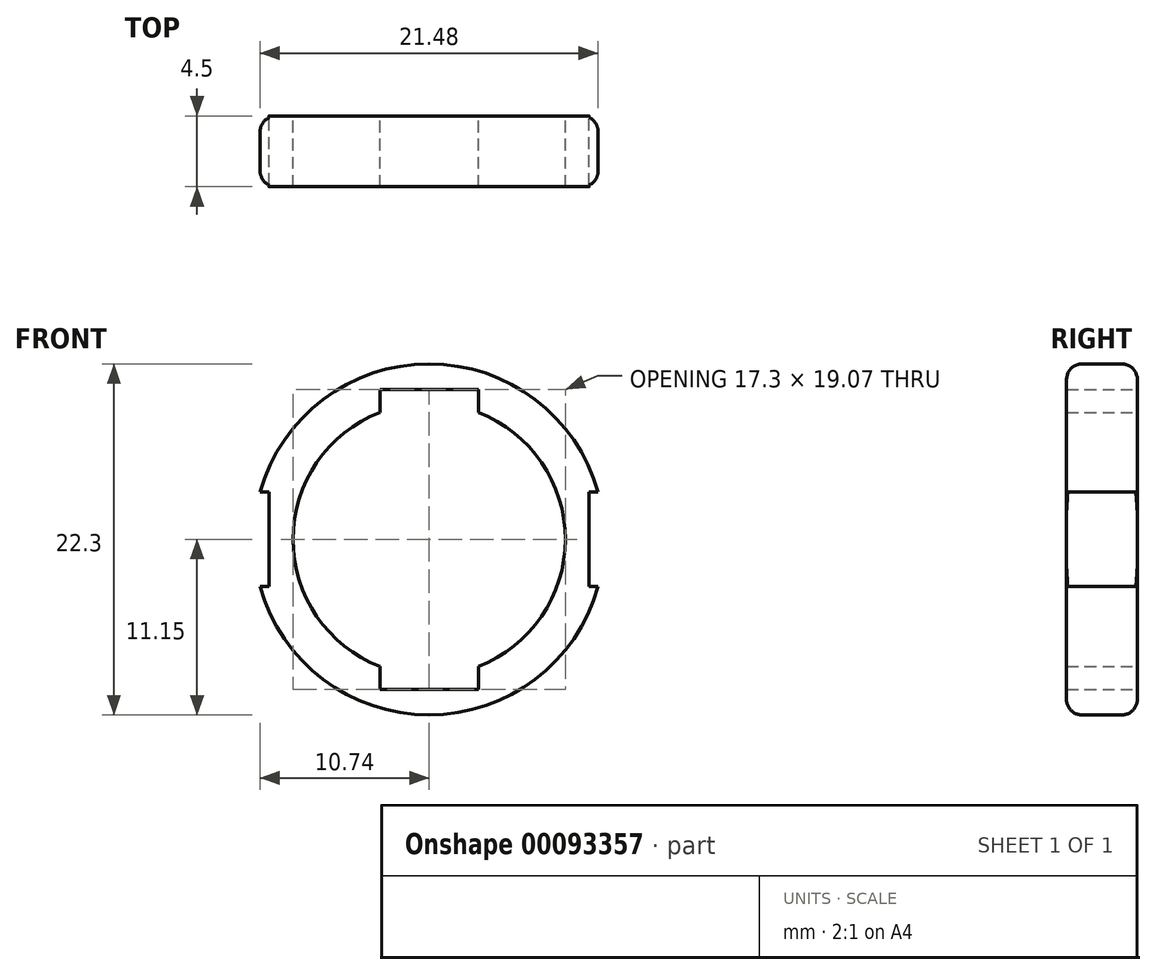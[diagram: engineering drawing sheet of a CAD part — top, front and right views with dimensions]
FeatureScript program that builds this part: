
annotation { "Feature Type Name" : "Feature", "Feature Type Description" : "" }
export const myFeature = defineFeature(function(context is Context, id is Id, definition is map)
    precondition{}
    {
        {
            var Q0;
            Q0=qCreatedBy(makeId("Front.planeOp"),FACE);
            var sketch = newSketch(context, id + "F0", { "sketchPlane" : qUnion([Q0])});
            skCircle(sketch, "E0", {"center": v(0, 0) * mm, "radius": 8.65 * mm});
            skCircle(sketch, "E1.0", {"center": v(0, 0) * mm, "radius": 11.15 * mm});
            skPoint(sketch, "E2", {"position": v(11.15, 0) * mm});
            skPoint(sketch, "E3", {"position": v(-11.15, 0) * mm});
            skLineSegment(sketch, "E4", {"start": v(11.15, 0) * mm, "end": v(11.15, 11.15) * mm});
            skLineSegment(sketch, "E5", {"start": v(11.15, 11.15) * mm, "end": v(0, 11.15) * mm});
            skLineSegment(sketch, "E6.MirrorCS", {"start": v(-11.15, 11.15) * mm, "end": v(0, 11.15) * mm});
            skLineSegment(sketch, "E7.MirrorCS", {"start": v(-11.15, 0) * mm, "end": v(-11.15, 11.15) * mm});
            skSolve(sketch);
        }
        {
            var Q0;
            Q0=makeQuery(id+"F0.imprint","IMPRINT",FACE,{"disambiguationData":[TD([[makeQuery(id+"F0.imprint","IMPRINT",EDGE,{"derivedFrom":sQuery(id+"F0.wireOp",EDGE,"E0")}),-1.0]])]});
            extrude(context, id + "F1", {"entities" : qUnion([Q0]), "depth" : 2.25 * mm, "hasSecondDirection" : true, "secondDirectionOppositeDirection" : true, "secondDirectionDepth" : 2.25 * mm});
        }
        {
            var Q0;
            Q0=makeQuery(id+"F1.opExtrude","CAP_EDGE",EDGE,{"disambiguationData":[OSD([sQuery(id+"F0.wireOp",EDGE,"E1.0")])],"isStart":false});
            var Q1;
            Q1=makeQuery(id+"F1.opExtrude","CAP_EDGE",EDGE,{"disambiguationData":[OSD([sQuery(id+"F0.wireOp",EDGE,"E1.0")])],"isStart":true});
            var Q2;
            Q2=makeQuery(id+"F1.opExtrude","CAP_EDGE",EDGE,{"disambiguationData":[OSD([sQuery(id+"F0.wireOp",EDGE,"E4")])],"isStart":false});
            var Q3;
            Q3=makeQuery(id+"F1.opExtrude","CAP_EDGE",EDGE,{"disambiguationData":[OSD([sQuery(id+"F0.wireOp",EDGE,"E4")])],"isStart":true});
            fillet(context, id + "F2", {"entities" : qUnion([Q0, Q1, Q2, Q3]), "radius" : 1 * mm, "tangentPropagation" : true, "allowEdgeOverflow" : false});
        }
        {
            var Q0;
            Q0=qCreatedBy(makeId("Front.planeOp"),FACE);
            var sketch = newSketch(context, id + "F3", { "sketchPlane" : qUnion([Q0])});
            skLineSegment(sketch, "E8.bottom", {"start": v(3.13, -9.54) * mm, "end": v(-3.13, -9.54) * mm});
            skLineSegment(sketch, "E8.top", {"start": v(3.13, 9.54) * mm, "end": v(-3.13, 9.54) * mm});
            skLineSegment(sketch, "E8.left", {"start": v(3.13, -9.54) * mm, "end": v(3.13, 9.54) * mm});
            skLineSegment(sketch, "E8.right", {"start": v(-3.13, -9.54) * mm, "end": v(-3.13, 9.54) * mm});
            skPoint(sketch, "E8.middle", {"position": v(0, 0) * mm});
            skLineSegment(sketch, "E9.bottom", {"start": v(11.87, 3) * mm, "end": v(10.17, 3) * mm});
            skLineSegment(sketch, "E9.top", {"start": v(11.87, -3) * mm, "end": v(10.17, -3) * mm});
            skLineSegment(sketch, "E9.left", {"start": v(11.87, 3) * mm, "end": v(11.87, -3) * mm});
            skLineSegment(sketch, "E9.right", {"start": v(10.17, 3) * mm, "end": v(10.17, -3) * mm});
            skPoint(sketch, "E9.middle", {"position": v(11.02, 0) * mm});
            skLineSegment(sketch, "E10.MirrorCS", {"start": v(-11.87, -3) * mm, "end": v(-10.17, -3) * mm});
            skLineSegment(sketch, "E11.MirrorCS", {"start": v(-10.17, 3) * mm, "end": v(-10.17, -3) * mm});
            skLineSegment(sketch, "E12.MirrorCS", {"start": v(-11.87, 3) * mm, "end": v(-11.87, -3) * mm});
            skLineSegment(sketch, "E13.MirrorCS", {"start": v(-11.87, 3) * mm, "end": v(-10.17, 3) * mm});
            skSolve(sketch);
        }
        {
            var Q0;
            Q0 = qSketchRegion(id + "F3", true);
            extrude(context, id + "F4", {"entities" : qUnion([Q0]), "operationType" : NewBodyOperationType.REMOVE, "depth" : 25 * mm, "hasSecondDirection" : true, "secondDirectionOppositeDirection" : true, "secondDirectionDepth" : 25 * mm});
        }
    });
